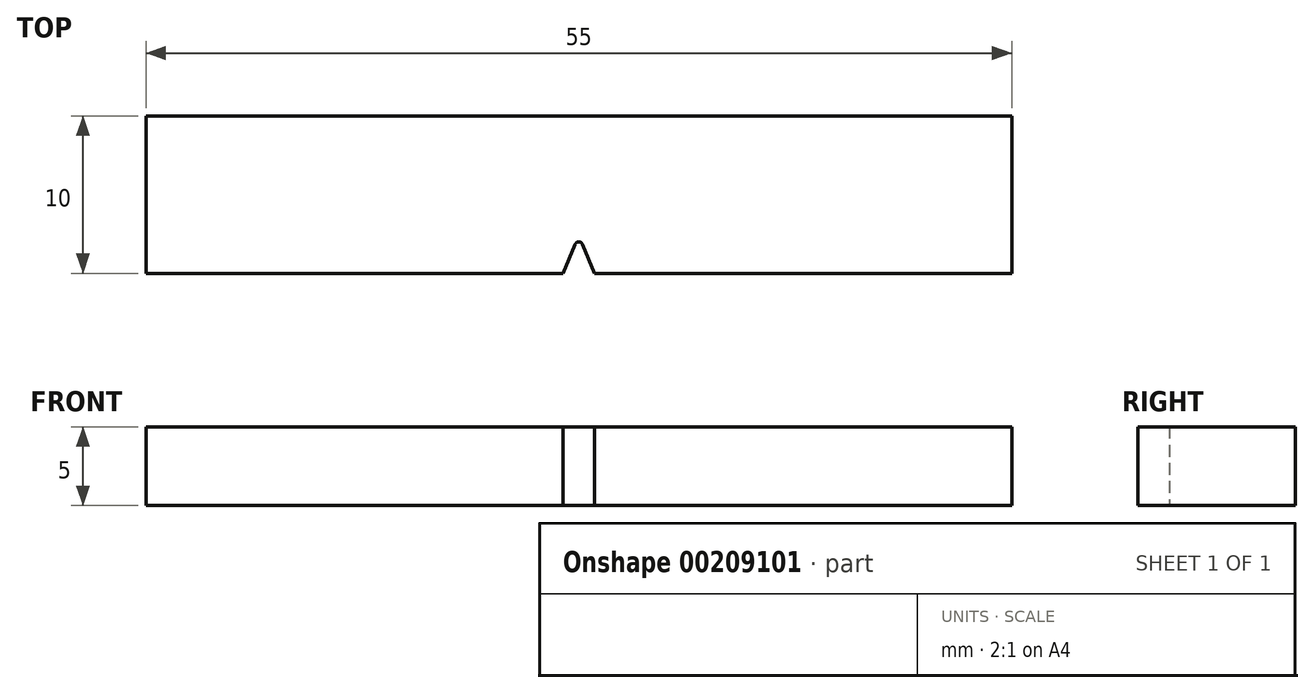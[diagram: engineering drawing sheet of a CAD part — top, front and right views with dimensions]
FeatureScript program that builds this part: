
annotation { "Feature Type Name" : "Feature", "Feature Type Description" : "" }
export const myFeature = defineFeature(function(context is Context, id is Id, definition is map)
    precondition{}
    {
        {
            var Q0;
            Q0=qCreatedBy(makeId("Top.planeOp"),FACE);
            var sketch = newSketch(context, id + "F0", { "sketchPlane" : qUnion([Q0])});
            skLineSegment(sketch, "E0.top", {"start": v(27.5, 5) * mm, "end": v(-27.5, 5) * mm});
            skLineSegment(sketch, "E0.left", {"start": v(27.5, -5) * mm, "end": v(27.5, 5) * mm});
            skLineSegment(sketch, "E0.right", {"start": v(-27.5, -5) * mm, "end": v(-27.5, 5) * mm});
            skPoint(sketch, "E0.middle", {"position": v(0, 0) * mm});
            skLineSegment(sketch, "E1", {"start": v(-1, -5) * mm, "end": v(-0.23, -3.15) * mm});
            skPoint(sketch, "E1.endSnap0", {"position": v(0, -5) * mm});
            skLineSegment(sketch, "E2", {"start": v(0.23, -3.15) * mm, "end": v(1, -5) * mm});
            skPoint(sketch, "E3.visualSharp", {"position": v(0, -2.6) * mm});
            skArc(sketch, "E3.filletArc", {"start": v(0.23, -3.15) * mm, "mid": v(0, -3) * mm, "end": v(-0.23, -3.15) * mm});
            skLineSegment(sketch, "E4", {"start": v(-27.5, -5) * mm, "end": v(-1, -5) * mm});
            skLineSegment(sketch, "E5", {"start": v(1, -5) * mm, "end": v(27.5, -5) * mm});
            skSolve(sketch);
        }
        {
            var Q0;
            Q0=makeQuery(id+"F0.imprint","IMPRINT",FACE,{"disambiguationData":[TD([[makeQuery(id+"F0.imprint","IMPRINT",EDGE,{"derivedFrom":sQuery(id+"F0.wireOp",EDGE,"E0.top")}),1.0]])]});
            extrude(context, id + "F1", {"entities" : qUnion([Q0]), "depth" : 5 * mm, "symmetric" : true});
        }
    });
